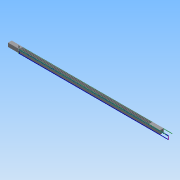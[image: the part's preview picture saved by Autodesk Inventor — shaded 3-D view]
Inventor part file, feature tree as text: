
AUTODESK INVENTOR PART (.ipt)
format: ipt  version: 2015 (Build 190159000, 159)  size: 2,281,984 bytes
history: native  units: in
note: dims shown in document units (in); Inventor stores cm internally (conversion verified against a paired STEP export)
features: sketch x6, other x4, extrude x3, projected_geometry x3, direct_edit x2, imported_body x1
ambient origin geometry x8: Origin, YZ Plane, XZ Plane, XY Plane, X Axis, Y Axis, Z Axis, Center Point
bodies: Body1 (feature_tree)
feature tree (19):
  parser-record x1  (decoder bookkeeping rows leaked as tree rows — omitted from the tree; the rows remain in map.json)
  other  "KKS10-10-51"
  sketch  "Sketch1"  dims[d2=0.0394in d6=-3.937in]
  direct_edit  "Direct Edit1"
  direct_edit  "Direct Edit2"
  sketch  "Sketch4"  dims[d7=-3.937in d10=0.0394in]
  sketch  "Sketch5"  dims[d11=0.3937in d12=1.1811in]
  extrude  "Extrusion1"  [1 undecoded]
  extrude  "Extrusion3"  Depth=0.0394in
  extrude  "Extrusion4"  Depth=1.1811in
  imported_body  "Base1"
  projected_geometry  "Projected Loop1"
  projected_geometry  "Projected Loop4"
  sketch  "Sketch6"  dims[d13=0.3937in d14=0.0in]
  sketch  "Sketch8"  dims[d19=0.7874in]
  sketch  "Sketch9"  dims[d20=13.7795in d21=0.3937in d22=0.0in d23=0.3937in d24=1.1811in d25=0.3937in d26=0.0in]
  projected_geometry  "Projected Loop6"
  other  "Size1"
  other  "Size2"
note: 1 required parameter value undecoded (feature->parameter linkage not recoverable at this tier; creation-order binding heuristic only, values carry confidence <= 0.55)
